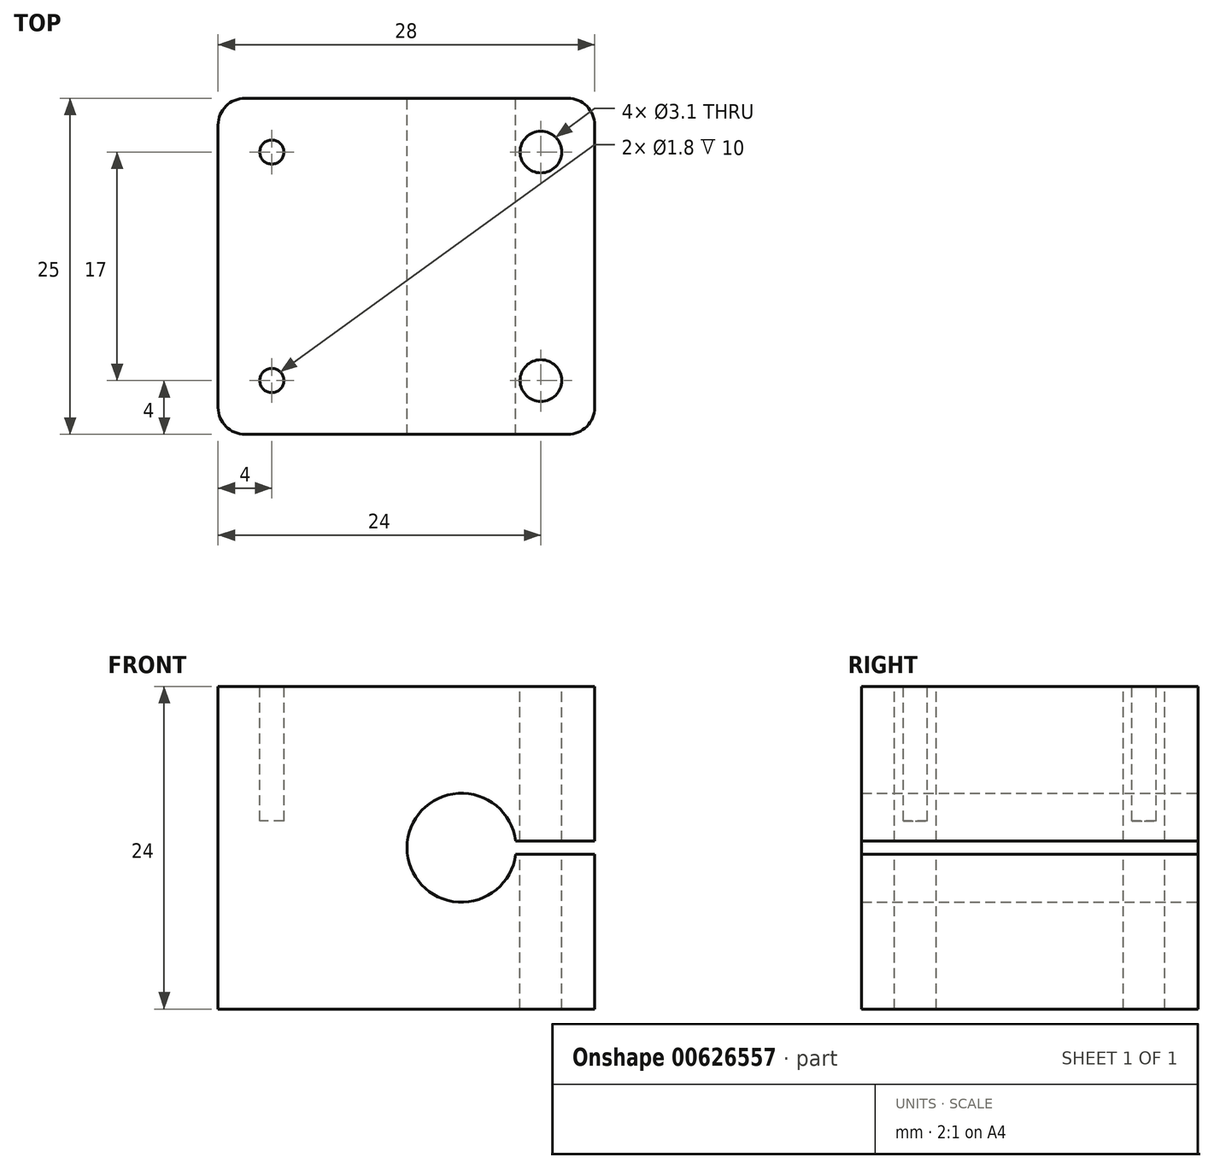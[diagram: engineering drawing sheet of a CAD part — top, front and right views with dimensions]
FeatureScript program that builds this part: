
annotation { "Feature Type Name" : "Feature", "Feature Type Description" : "" }
export const myFeature = defineFeature(function(context is Context, id is Id, definition is map)
    precondition{}
    {
        {
            var Q0;
            Q0=qCreatedBy(makeId("Front.planeOp"),FACE);
            var sketch = newSketch(context, id + "F0", { "sketchPlane" : qUnion([Q0])});
            skLineSegment(sketch, "E0.bottom", {"start": v(14, -12) * mm, "end": v(-14, -12) * mm});
            skLineSegment(sketch, "E0.top", {"start": v(14, 12) * mm, "end": v(-14, 12) * mm});
            skLineSegment(sketch, "E0.left", {"start": v(14, -12) * mm, "end": v(14, 12) * mm});
            skLineSegment(sketch, "E0.right", {"start": v(-14, -12) * mm, "end": v(-14, 12) * mm});
            skPoint(sketch, "E0.middle", {"position": v(0, 0) * mm});
            skCircle(sketch, "E1", {"center": v(4.1, 0) * mm, "radius": 4.05 * mm});
            skLineSegment(sketch, "E2", {"start": v(8.12, -0.5) * mm, "end": v(14, -0.5) * mm});
            skLineSegment(sketch, "E3", {"start": v(8.12, 0.5) * mm, "end": v(14, 0.5) * mm});
            skLineSegment(sketch, "E4", {"start": v(4.1, 0) * mm, "end": v(14, 0) * mm, "construction": true});
            skSolve(sketch);
        }
        {
            var Q0;
            Q0=makeQuery(id+"F0.imprint","IMPRINT",FACE,{"disambiguationData":[TD([[makeQuery(id+"F0.imprint","IMPRINT",EDGE,{"derivedFrom":sQuery(id+"F0.wireOp",EDGE,"E0.bottom")}),-1.0]])]});
            extrude(context, id + "F1", {"entities" : qUnion([Q0]), "depth" : 25 * mm, "offsetDistance" : 25 * mm});
        }
        {
            var Q0;
            Q0=makeQuery(id+"F1.opExtrude","SWEPT_FACE",FACE,{"disambiguationData":[OSD([sQuery(id+"F0.wireOp",EDGE,"E0.top")])]});
            var sketch = newSketch(context, id + "F2", { "sketchPlane" : qUnion([Q0])});
            skLineSegment(sketch, "E5.bottom", {"start": v(10, -21) * mm, "end": v(-10, -21) * mm, "construction": true});
            skLineSegment(sketch, "E5.top", {"start": v(10, -4) * mm, "end": v(-10, -4) * mm, "construction": true});
            skLineSegment(sketch, "E5.left", {"start": v(10, -21) * mm, "end": v(10, -4) * mm, "construction": true});
            skLineSegment(sketch, "E5.right", {"start": v(-10, -21) * mm, "end": v(-10, -4) * mm, "construction": true});
            skPoint(sketch, "E5.middle", {"position": v(0, -12.5) * mm});
            skPoint(sketch, "E5.middle.positionSnap0", {"position": v(-14, -12.5) * mm});
            skPoint(sketch, "E5.centerSnap0", {"position": v(-14, -12.5) * mm});
            skCircle(sketch, "E6", {"center": v(-10, -4) * mm, "radius": 0.9 * mm});
            skCircle(sketch, "E7", {"center": v(-10, -21) * mm, "radius": 0.9 * mm});
            skCircle(sketch, "E8", {"center": v(10, -4) * mm, "radius": 1.55 * mm});
            skCircle(sketch, "E9", {"center": v(10, -21) * mm, "radius": 1.55 * mm});
            skSolve(sketch);
        }
        {
            var Q0;
            Q0=makeQuery(id+"F2.imprint","IMPRINT",FACE,{"disambiguationData":[TD([[makeQuery(id+"F2.imprint","IMPRINT",EDGE,{"derivedFrom":sQuery(id+"F2.wireOp",EDGE,"E6")}),1.0]])]});
            var Q1;
            Q1=makeQuery(id+"F2.imprint","IMPRINT",FACE,{"disambiguationData":[TD([[makeQuery(id+"F2.imprint","IMPRINT",EDGE,{"derivedFrom":sQuery(id+"F2.wireOp",EDGE,"E7")}),1.0]])]});
            extrude(context, id + "F3", {"entities" : qUnion([Q0, Q1]), "operationType" : NewBodyOperationType.REMOVE, "oppositeDirection" : true, "depth" : 10 * mm, "offsetDistance" : 25 * mm});
        }
        {
            var Q0;
            Q0=makeQuery(id+"F2.imprint","IMPRINT",FACE,{"disambiguationData":[TD([[makeQuery(id+"F2.imprint","IMPRINT",EDGE,{"derivedFrom":sQuery(id+"F2.wireOp",EDGE,"E9")}),1.0]])]});
            var Q1;
            Q1=makeQuery(id+"F2.imprint","IMPRINT",FACE,{"disambiguationData":[TD([[makeQuery(id+"F2.imprint","IMPRINT",EDGE,{"derivedFrom":sQuery(id+"F2.wireOp",EDGE,"E8")}),1.0]])]});
            extrude(context, id + "F4", {"entities" : qUnion([Q0, Q1]), "operationType" : NewBodyOperationType.REMOVE, "endBound" : BoundingType.THROUGH_ALL, "oppositeDirection" : true, "depth" : 25 * mm, "offsetDistance" : 25 * mm});
        }
        {
            var Q0;
            Q0=makeQuery(id+"F1.opExtrude","CAP_EDGE",EDGE,{"disambiguationData":[OSD([sQuery(id+"F0.wireOp",EDGE,"E0.right")])],"isStart":true});
            var Q1;
            {var subQ0=sQuery(id+"F0.wireOp",EDGE,"E0.left");Q1=makeQuery(id+"F1.opExtrude","CAP_EDGE",EDGE,{"disambiguationData":[OSD([subQ0]),TDD([makeQuery(id+"F0.imprint","IMPRINT",EDGE,{"disambiguationData":[TD([[makeQuery(id+"F0.imprint","INTERSECT",VERTEX,{"derivedFrom":[sQuery(id+"F0.wireOp",EDGE,"E0.bottom"),subQ0]}),-1.0]])],"derivedFrom":subQ0})])],"isStart":false});}
            var Q2;
            {var subQ0=sQuery(id+"F0.wireOp",EDGE,"E0.left");Q2=makeQuery(id+"F1.opExtrude","CAP_EDGE",EDGE,{"disambiguationData":[OSD([subQ0]),TDD([makeQuery(id+"F0.imprint","IMPRINT",EDGE,{"disambiguationData":[TD([[makeQuery(id+"F0.imprint","INTERSECT",VERTEX,{"derivedFrom":[sQuery(id+"F0.wireOp",EDGE,"E0.top"),subQ0]}),1.0]])],"derivedFrom":subQ0})])],"isStart":false});}
            var Q3;
            {var subQ0=sQuery(id+"F0.wireOp",EDGE,"E0.left");Q3=makeQuery(id+"F1.opExtrude","CAP_EDGE",EDGE,{"disambiguationData":[OSD([subQ0]),TDD([makeQuery(id+"F0.imprint","IMPRINT",EDGE,{"disambiguationData":[TD([[makeQuery(id+"F0.imprint","INTERSECT",VERTEX,{"derivedFrom":[sQuery(id+"F0.wireOp",EDGE,"E0.top"),subQ0]}),1.0]])],"derivedFrom":subQ0})])],"isStart":true});}
            var Q4;
            {var subQ0=sQuery(id+"F0.wireOp",EDGE,"E0.left");Q4=makeQuery(id+"F1.opExtrude","CAP_EDGE",EDGE,{"disambiguationData":[OSD([subQ0]),TDD([makeQuery(id+"F0.imprint","IMPRINT",EDGE,{"disambiguationData":[TD([[makeQuery(id+"F0.imprint","INTERSECT",VERTEX,{"derivedFrom":[sQuery(id+"F0.wireOp",EDGE,"E0.bottom"),subQ0]}),-1.0]])],"derivedFrom":subQ0})])],"isStart":true});}
            var Q5;
            Q5=makeQuery(id+"F1.opExtrude","CAP_EDGE",EDGE,{"disambiguationData":[OSD([sQuery(id+"F0.wireOp",EDGE,"E0.right")])],"isStart":false});
            fillet(context, id + "F5", {"entities" : qUnion([Q0, Q1, Q2, Q3, Q4, Q5]), "radius" : 2 * mm, "tangentPropagation" : true, "allowEdgeOverflow" : false});
        }
    });
